# Revit family: Фонарь уличный «Адмирал - 3» со светильниками Арт 9813
name_source: partatom
category: Антураж
revit_build: Autodesk Revit 2018 (Build: 20180423_1000(x64)
units: mm (PartAtom-declared; Revit-internal decimal feet)

## family parameters
Всегда вертикально = Да
Источник визуального образа = Геометрия семейства
На основе рабочей плоскости = Нет
Общий = Нет
При загрузке вырезать с полостями = Нет
Точка расчета площади = Нет

## types (6) — shared parameters
URL = https://hobbyka.ru
Артикул товара = Арт. 9813
Группа модели = Светильники с чугунными опорами
Длина = 1300 мм
Изготовитель = ООО «Хоббика»
Изображение типоразмера = Фонарь уличный «Адмирал - 3» со светильниками Арт 9813.jpg
Материал изделия = Сталь, поликарбонат
Цвет основания = Сталь
Ширина = 360 мм

## per-type parameters (varying)
| type | Версия 4,0 м | Версия 4,5 м | Версия 5,0 м | Версия 5,5 м | Версия 6,0 м | Высота | Высота столба | Описание |
| Версия 4,0 м | Да | Нет | Нет | Нет | Нет | 4000 мм | 2500 мм | Фонарь уличный «Адмирал - 3» со светильниками. Версия 4,0 м |
| Версия 4,5 м | Нет | Да | Нет | Нет | Нет | 4500 мм | 3000 мм | Фонарь уличный «Адмирал - 3» со светильниками. Версия 4,5 м |
| Версия 5,0 м | Нет | Нет | Да | Нет | Нет | 5000 мм | 3500 мм | Фонарь уличный «Адмирал - 3» со светильниками. Версия 5,0 м |
| Версия 5,5 м | Нет | Нет | Нет | Да | Нет | 5500 мм | 4000 мм | Фонарь уличный «Адмирал - 3» со светильниками. Версия 5,5 м |
| Версия 6,0 м | Нет | Нет | Нет | Нет | Да | 6000 мм | 4500 мм | Фонарь уличный «Адмирал - 3» со светильниками. Версия 6,0 м |
| Версия 6,5 м | Нет | Нет | Нет | Нет | Нет | 6500 мм | 5000 мм | Фонарь уличный «Адмирал - 3» со светильниками. Версия 6,5 м |
